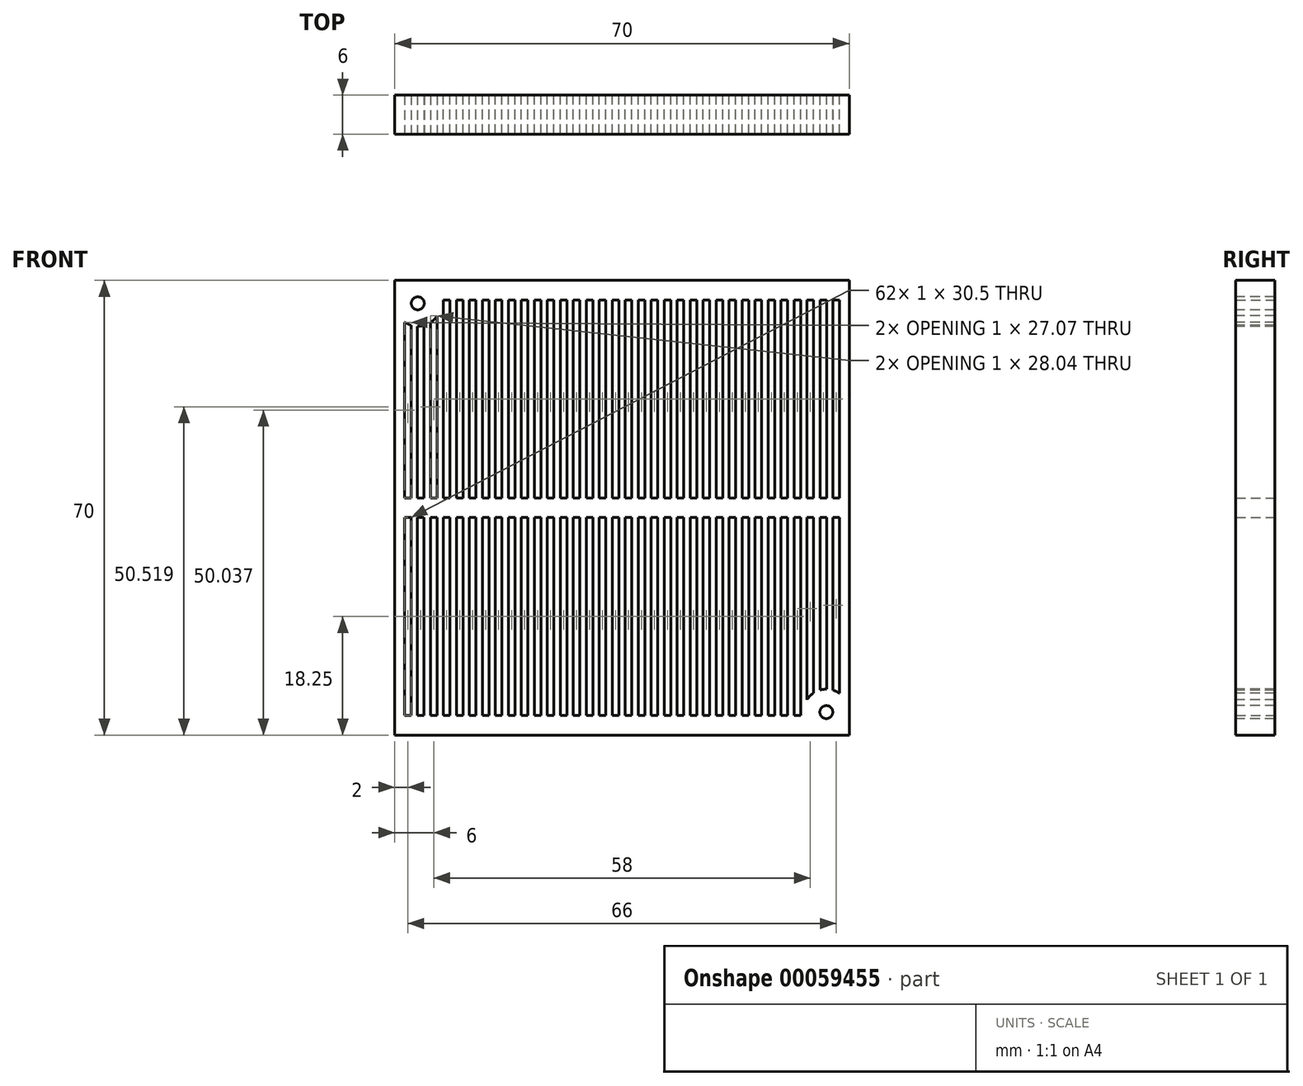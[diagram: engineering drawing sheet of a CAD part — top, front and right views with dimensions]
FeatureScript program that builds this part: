
annotation { "Feature Type Name" : "Feature", "Feature Type Description" : "" }
export const myFeature = defineFeature(function(context is Context, id is Id, definition is map)
    precondition{}
    {
        {
            var Q0;
            Q0=qCreatedBy(makeId("Front.planeOp"),FACE);
            var sketch = newSketch(context, id + "F0", { "sketchPlane" : qUnion([Q0])});
            skLineSegment(sketch, "E0.bottom", {"start": v(0, 70) * mm, "end": v(70, 70) * mm});
            skLineSegment(sketch, "E0.top", {"start": v(0, 0) * mm, "end": v(70, 0) * mm});
            skLineSegment(sketch, "E0.left", {"start": v(0, 70) * mm, "end": v(0, 0) * mm});
            skLineSegment(sketch, "E0.right", {"start": v(70, 70) * mm, "end": v(70, 0) * mm});
            skLineSegment(sketch, "E1.bottom", {"start": v(1.5, 67) * mm, "end": v(2.5, 67) * mm});
            skLineSegment(sketch, "E1.top", {"start": v(1.5, 36.5) * mm, "end": v(2.5, 36.5) * mm});
            skLineSegment(sketch, "E1.left", {"start": v(1.5, 67) * mm, "end": v(1.5, 36.5) * mm});
            skLineSegment(sketch, "E1.right", {"start": v(2.5, 67) * mm, "end": v(2.5, 36.5) * mm});
            skLineSegment(sketch, "E2.bottom", {"start": v(1.5, 33.5) * mm, "end": v(2.5, 33.5) * mm});
            skLineSegment(sketch, "E2.top", {"start": v(1.5, 3) * mm, "end": v(2.5, 3) * mm});
            skLineSegment(sketch, "E2.left", {"start": v(1.5, 33.5) * mm, "end": v(1.5, 3) * mm});
            skLineSegment(sketch, "E2.right", {"start": v(2.5, 33.5) * mm, "end": v(2.5, 3) * mm});
            skLineSegment(sketch, "E3.1.0.0", {"start": v(4.5, 67) * mm, "end": v(4.5, 36.5) * mm});
            skLineSegment(sketch, "E3.1.0.1", {"start": v(4.5, 33.5) * mm, "end": v(4.5, 3) * mm});
            skLineSegment(sketch, "E3.1.0.2", {"start": v(3.5, 33.5) * mm, "end": v(4.5, 33.5) * mm});
            skLineSegment(sketch, "E3.1.0.3", {"start": v(3.5, 33.5) * mm, "end": v(3.5, 3) * mm});
            skLineSegment(sketch, "E3.1.0.4", {"start": v(3.5, 3) * mm, "end": v(4.5, 3) * mm});
            skLineSegment(sketch, "E3.1.0.5", {"start": v(3.5, 67) * mm, "end": v(3.5, 36.5) * mm});
            skLineSegment(sketch, "E3.1.0.6", {"start": v(3.5, 67) * mm, "end": v(4.5, 67) * mm});
            skLineSegment(sketch, "E3.1.0.7", {"start": v(3.5, 36.5) * mm, "end": v(4.5, 36.5) * mm});
            skLineSegment(sketch, "E3.2.0.0", {"start": v(6.5, 67) * mm, "end": v(6.5, 36.5) * mm});
            skLineSegment(sketch, "E3.2.0.1", {"start": v(6.5, 33.5) * mm, "end": v(6.5, 3) * mm});
            skLineSegment(sketch, "E3.2.0.2", {"start": v(5.5, 33.5) * mm, "end": v(6.5, 33.5) * mm});
            skLineSegment(sketch, "E3.2.0.3", {"start": v(5.5, 33.5) * mm, "end": v(5.5, 3) * mm});
            skLineSegment(sketch, "E3.2.0.4", {"start": v(5.5, 3) * mm, "end": v(6.5, 3) * mm});
            skLineSegment(sketch, "E3.2.0.5", {"start": v(5.5, 67) * mm, "end": v(5.5, 36.5) * mm});
            skLineSegment(sketch, "E3.2.0.6", {"start": v(5.5, 67) * mm, "end": v(6.5, 67) * mm});
            skLineSegment(sketch, "E3.2.0.7", {"start": v(5.5, 36.5) * mm, "end": v(6.5, 36.5) * mm});
            skLineSegment(sketch, "E3.3.0.0", {"start": v(8.5, 67) * mm, "end": v(8.5, 36.5) * mm});
            skLineSegment(sketch, "E3.3.0.1", {"start": v(8.5, 33.5) * mm, "end": v(8.5, 3) * mm});
            skLineSegment(sketch, "E3.3.0.2", {"start": v(7.5, 33.5) * mm, "end": v(8.5, 33.5) * mm});
            skLineSegment(sketch, "E3.3.0.3", {"start": v(7.5, 33.5) * mm, "end": v(7.5, 3) * mm});
            skLineSegment(sketch, "E3.3.0.4", {"start": v(7.5, 3) * mm, "end": v(8.5, 3) * mm});
            skLineSegment(sketch, "E3.3.0.5", {"start": v(7.5, 67) * mm, "end": v(7.5, 36.5) * mm});
            skLineSegment(sketch, "E3.3.0.6", {"start": v(7.5, 67) * mm, "end": v(8.5, 67) * mm});
            skLineSegment(sketch, "E3.3.0.7", {"start": v(7.5, 36.5) * mm, "end": v(8.5, 36.5) * mm});
            skLineSegment(sketch, "E3.4.0.0", {"start": v(10.5, 67) * mm, "end": v(10.5, 36.5) * mm});
            skLineSegment(sketch, "E3.4.0.1", {"start": v(10.5, 33.5) * mm, "end": v(10.5, 3) * mm});
            skLineSegment(sketch, "E3.4.0.2", {"start": v(9.5, 33.5) * mm, "end": v(10.5, 33.5) * mm});
            skLineSegment(sketch, "E3.4.0.3", {"start": v(9.5, 33.5) * mm, "end": v(9.5, 3) * mm});
            skLineSegment(sketch, "E3.4.0.4", {"start": v(9.5, 3) * mm, "end": v(10.5, 3) * mm});
            skLineSegment(sketch, "E3.4.0.5", {"start": v(9.5, 67) * mm, "end": v(9.5, 36.5) * mm});
            skLineSegment(sketch, "E3.4.0.6", {"start": v(9.5, 67) * mm, "end": v(10.5, 67) * mm});
            skLineSegment(sketch, "E3.4.0.7", {"start": v(9.5, 36.5) * mm, "end": v(10.5, 36.5) * mm});
            skLineSegment(sketch, "E3.5.0.0", {"start": v(12.5, 67) * mm, "end": v(12.5, 36.5) * mm});
            skLineSegment(sketch, "E3.5.0.1", {"start": v(12.5, 33.5) * mm, "end": v(12.5, 3) * mm});
            skLineSegment(sketch, "E3.5.0.2", {"start": v(11.5, 33.5) * mm, "end": v(12.5, 33.5) * mm});
            skLineSegment(sketch, "E3.5.0.3", {"start": v(11.5, 33.5) * mm, "end": v(11.5, 3) * mm});
            skLineSegment(sketch, "E3.5.0.4", {"start": v(11.5, 3) * mm, "end": v(12.5, 3) * mm});
            skLineSegment(sketch, "E3.5.0.5", {"start": v(11.5, 67) * mm, "end": v(11.5, 36.5) * mm});
            skLineSegment(sketch, "E3.5.0.6", {"start": v(11.5, 67) * mm, "end": v(12.5, 67) * mm});
            skLineSegment(sketch, "E3.5.0.7", {"start": v(11.5, 36.5) * mm, "end": v(12.5, 36.5) * mm});
            skLineSegment(sketch, "E3.6.0.0", {"start": v(14.5, 67) * mm, "end": v(14.5, 36.5) * mm});
            skLineSegment(sketch, "E3.6.0.1", {"start": v(14.5, 33.5) * mm, "end": v(14.5, 3) * mm});
            skLineSegment(sketch, "E3.6.0.2", {"start": v(13.5, 33.5) * mm, "end": v(14.5, 33.5) * mm});
            skLineSegment(sketch, "E3.6.0.3", {"start": v(13.5, 33.5) * mm, "end": v(13.5, 3) * mm});
            skLineSegment(sketch, "E3.6.0.4", {"start": v(13.5, 3) * mm, "end": v(14.5, 3) * mm});
            skLineSegment(sketch, "E3.6.0.5", {"start": v(13.5, 67) * mm, "end": v(13.5, 36.5) * mm});
            skLineSegment(sketch, "E3.6.0.6", {"start": v(13.5, 67) * mm, "end": v(14.5, 67) * mm});
            skLineSegment(sketch, "E3.6.0.7", {"start": v(13.5, 36.5) * mm, "end": v(14.5, 36.5) * mm});
            skLineSegment(sketch, "E3.7.0.0", {"start": v(16.5, 67) * mm, "end": v(16.5, 36.5) * mm});
            skLineSegment(sketch, "E3.7.0.1", {"start": v(16.5, 33.5) * mm, "end": v(16.5, 3) * mm});
            skLineSegment(sketch, "E3.7.0.2", {"start": v(15.5, 33.5) * mm, "end": v(16.5, 33.5) * mm});
            skLineSegment(sketch, "E3.7.0.3", {"start": v(15.5, 33.5) * mm, "end": v(15.5, 3) * mm});
            skLineSegment(sketch, "E3.7.0.4", {"start": v(15.5, 3) * mm, "end": v(16.5, 3) * mm});
            skLineSegment(sketch, "E3.7.0.5", {"start": v(15.5, 67) * mm, "end": v(15.5, 36.5) * mm});
            skLineSegment(sketch, "E3.7.0.6", {"start": v(15.5, 67) * mm, "end": v(16.5, 67) * mm});
            skLineSegment(sketch, "E3.7.0.7", {"start": v(15.5, 36.5) * mm, "end": v(16.5, 36.5) * mm});
            skLineSegment(sketch, "E3.8.0.0", {"start": v(18.5, 67) * mm, "end": v(18.5, 36.5) * mm});
            skLineSegment(sketch, "E3.8.0.1", {"start": v(18.5, 33.5) * mm, "end": v(18.5, 3) * mm});
            skLineSegment(sketch, "E3.8.0.2", {"start": v(17.5, 33.5) * mm, "end": v(18.5, 33.5) * mm});
            skLineSegment(sketch, "E3.8.0.3", {"start": v(17.5, 33.5) * mm, "end": v(17.5, 3) * mm});
            skLineSegment(sketch, "E3.8.0.4", {"start": v(17.5, 3) * mm, "end": v(18.5, 3) * mm});
            skLineSegment(sketch, "E3.8.0.5", {"start": v(17.5, 67) * mm, "end": v(17.5, 36.5) * mm});
            skLineSegment(sketch, "E3.8.0.6", {"start": v(17.5, 67) * mm, "end": v(18.5, 67) * mm});
            skLineSegment(sketch, "E3.8.0.7", {"start": v(17.5, 36.5) * mm, "end": v(18.5, 36.5) * mm});
            skLineSegment(sketch, "E3.9.0.0", {"start": v(20.5, 67) * mm, "end": v(20.5, 36.5) * mm});
            skLineSegment(sketch, "E3.9.0.1", {"start": v(20.5, 33.5) * mm, "end": v(20.5, 3) * mm});
            skLineSegment(sketch, "E3.9.0.2", {"start": v(19.5, 33.5) * mm, "end": v(20.5, 33.5) * mm});
            skLineSegment(sketch, "E3.9.0.3", {"start": v(19.5, 33.5) * mm, "end": v(19.5, 3) * mm});
            skLineSegment(sketch, "E3.9.0.4", {"start": v(19.5, 3) * mm, "end": v(20.5, 3) * mm});
            skLineSegment(sketch, "E3.9.0.5", {"start": v(19.5, 67) * mm, "end": v(19.5, 36.5) * mm});
            skLineSegment(sketch, "E3.9.0.6", {"start": v(19.5, 67) * mm, "end": v(20.5, 67) * mm});
            skLineSegment(sketch, "E3.9.0.7", {"start": v(19.5, 36.5) * mm, "end": v(20.5, 36.5) * mm});
            skLineSegment(sketch, "E3.10.0.0", {"start": v(22.5, 67) * mm, "end": v(22.5, 36.5) * mm});
            skLineSegment(sketch, "E3.10.0.1", {"start": v(22.5, 33.5) * mm, "end": v(22.5, 3) * mm});
            skLineSegment(sketch, "E3.10.0.2", {"start": v(21.5, 33.5) * mm, "end": v(22.5, 33.5) * mm});
            skLineSegment(sketch, "E3.10.0.3", {"start": v(21.5, 33.5) * mm, "end": v(21.5, 3) * mm});
            skLineSegment(sketch, "E3.10.0.4", {"start": v(21.5, 3) * mm, "end": v(22.5, 3) * mm});
            skLineSegment(sketch, "E3.10.0.5", {"start": v(21.5, 67) * mm, "end": v(21.5, 36.5) * mm});
            skLineSegment(sketch, "E3.10.0.6", {"start": v(21.5, 67) * mm, "end": v(22.5, 67) * mm});
            skLineSegment(sketch, "E3.10.0.7", {"start": v(21.5, 36.5) * mm, "end": v(22.5, 36.5) * mm});
            skLineSegment(sketch, "E3.11.0.0", {"start": v(24.5, 67) * mm, "end": v(24.5, 36.5) * mm});
            skLineSegment(sketch, "E3.11.0.1", {"start": v(24.5, 33.5) * mm, "end": v(24.5, 3) * mm});
            skLineSegment(sketch, "E3.11.0.2", {"start": v(23.5, 33.5) * mm, "end": v(24.5, 33.5) * mm});
            skLineSegment(sketch, "E3.11.0.3", {"start": v(23.5, 33.5) * mm, "end": v(23.5, 3) * mm});
            skLineSegment(sketch, "E3.11.0.4", {"start": v(23.5, 3) * mm, "end": v(24.5, 3) * mm});
            skLineSegment(sketch, "E3.11.0.5", {"start": v(23.5, 67) * mm, "end": v(23.5, 36.5) * mm});
            skLineSegment(sketch, "E3.11.0.6", {"start": v(23.5, 67) * mm, "end": v(24.5, 67) * mm});
            skLineSegment(sketch, "E3.11.0.7", {"start": v(23.5, 36.5) * mm, "end": v(24.5, 36.5) * mm});
            skLineSegment(sketch, "E3.12.0.0", {"start": v(26.5, 67) * mm, "end": v(26.5, 36.5) * mm});
            skLineSegment(sketch, "E3.12.0.1", {"start": v(26.5, 33.5) * mm, "end": v(26.5, 3) * mm});
            skLineSegment(sketch, "E3.12.0.2", {"start": v(25.5, 33.5) * mm, "end": v(26.5, 33.5) * mm});
            skLineSegment(sketch, "E3.12.0.3", {"start": v(25.5, 33.5) * mm, "end": v(25.5, 3) * mm});
            skLineSegment(sketch, "E3.12.0.4", {"start": v(25.5, 3) * mm, "end": v(26.5, 3) * mm});
            skLineSegment(sketch, "E3.12.0.5", {"start": v(25.5, 67) * mm, "end": v(25.5, 36.5) * mm});
            skLineSegment(sketch, "E3.12.0.6", {"start": v(25.5, 67) * mm, "end": v(26.5, 67) * mm});
            skLineSegment(sketch, "E3.12.0.7", {"start": v(25.5, 36.5) * mm, "end": v(26.5, 36.5) * mm});
            skLineSegment(sketch, "E3.13.0.0", {"start": v(28.5, 67) * mm, "end": v(28.5, 36.5) * mm});
            skLineSegment(sketch, "E3.13.0.1", {"start": v(28.5, 33.5) * mm, "end": v(28.5, 3) * mm});
            skLineSegment(sketch, "E3.13.0.2", {"start": v(27.5, 33.5) * mm, "end": v(28.5, 33.5) * mm});
            skLineSegment(sketch, "E3.13.0.3", {"start": v(27.5, 33.5) * mm, "end": v(27.5, 3) * mm});
            skLineSegment(sketch, "E3.13.0.4", {"start": v(27.5, 3) * mm, "end": v(28.5, 3) * mm});
            skLineSegment(sketch, "E3.13.0.5", {"start": v(27.5, 67) * mm, "end": v(27.5, 36.5) * mm});
            skLineSegment(sketch, "E3.13.0.6", {"start": v(27.5, 67) * mm, "end": v(28.5, 67) * mm});
            skLineSegment(sketch, "E3.13.0.7", {"start": v(27.5, 36.5) * mm, "end": v(28.5, 36.5) * mm});
            skLineSegment(sketch, "E3.14.0.0", {"start": v(30.5, 67) * mm, "end": v(30.5, 36.5) * mm});
            skLineSegment(sketch, "E3.14.0.1", {"start": v(30.5, 33.5) * mm, "end": v(30.5, 3) * mm});
            skLineSegment(sketch, "E3.14.0.2", {"start": v(29.5, 33.5) * mm, "end": v(30.5, 33.5) * mm});
            skLineSegment(sketch, "E3.14.0.3", {"start": v(29.5, 33.5) * mm, "end": v(29.5, 3) * mm});
            skLineSegment(sketch, "E3.14.0.4", {"start": v(29.5, 3) * mm, "end": v(30.5, 3) * mm});
            skLineSegment(sketch, "E3.14.0.5", {"start": v(29.5, 67) * mm, "end": v(29.5, 36.5) * mm});
            skLineSegment(sketch, "E3.14.0.6", {"start": v(29.5, 67) * mm, "end": v(30.5, 67) * mm});
            skLineSegment(sketch, "E3.14.0.7", {"start": v(29.5, 36.5) * mm, "end": v(30.5, 36.5) * mm});
            skLineSegment(sketch, "E3.15.0.0", {"start": v(32.5, 67) * mm, "end": v(32.5, 36.5) * mm});
            skLineSegment(sketch, "E3.15.0.1", {"start": v(32.5, 33.5) * mm, "end": v(32.5, 3) * mm});
            skLineSegment(sketch, "E3.15.0.2", {"start": v(31.5, 33.5) * mm, "end": v(32.5, 33.5) * mm});
            skLineSegment(sketch, "E3.15.0.3", {"start": v(31.5, 33.5) * mm, "end": v(31.5, 3) * mm});
            skLineSegment(sketch, "E3.15.0.4", {"start": v(31.5, 3) * mm, "end": v(32.5, 3) * mm});
            skLineSegment(sketch, "E3.15.0.5", {"start": v(31.5, 67) * mm, "end": v(31.5, 36.5) * mm});
            skLineSegment(sketch, "E3.15.0.6", {"start": v(31.5, 67) * mm, "end": v(32.5, 67) * mm});
            skLineSegment(sketch, "E3.15.0.7", {"start": v(31.5, 36.5) * mm, "end": v(32.5, 36.5) * mm});
            skLineSegment(sketch, "E3.16.0.0", {"start": v(34.5, 67) * mm, "end": v(34.5, 36.5) * mm});
            skLineSegment(sketch, "E3.16.0.1", {"start": v(34.5, 33.5) * mm, "end": v(34.5, 3) * mm});
            skLineSegment(sketch, "E3.16.0.2", {"start": v(33.5, 33.5) * mm, "end": v(34.5, 33.5) * mm});
            skLineSegment(sketch, "E3.16.0.3", {"start": v(33.5, 33.5) * mm, "end": v(33.5, 3) * mm});
            skLineSegment(sketch, "E3.16.0.4", {"start": v(33.5, 3) * mm, "end": v(34.5, 3) * mm});
            skLineSegment(sketch, "E3.16.0.5", {"start": v(33.5, 67) * mm, "end": v(33.5, 36.5) * mm});
            skLineSegment(sketch, "E3.16.0.6", {"start": v(33.5, 67) * mm, "end": v(34.5, 67) * mm});
            skLineSegment(sketch, "E3.16.0.7", {"start": v(33.5, 36.5) * mm, "end": v(34.5, 36.5) * mm});
            skLineSegment(sketch, "E3.17.0.0", {"start": v(36.5, 67) * mm, "end": v(36.5, 36.5) * mm});
            skLineSegment(sketch, "E3.17.0.1", {"start": v(36.5, 33.5) * mm, "end": v(36.5, 3) * mm});
            skLineSegment(sketch, "E3.17.0.2", {"start": v(35.5, 33.5) * mm, "end": v(36.5, 33.5) * mm});
            skLineSegment(sketch, "E3.17.0.3", {"start": v(35.5, 33.5) * mm, "end": v(35.5, 3) * mm});
            skLineSegment(sketch, "E3.17.0.4", {"start": v(35.5, 3) * mm, "end": v(36.5, 3) * mm});
            skLineSegment(sketch, "E3.17.0.5", {"start": v(35.5, 67) * mm, "end": v(35.5, 36.5) * mm});
            skLineSegment(sketch, "E3.17.0.6", {"start": v(35.5, 67) * mm, "end": v(36.5, 67) * mm});
            skLineSegment(sketch, "E3.17.0.7", {"start": v(35.5, 36.5) * mm, "end": v(36.5, 36.5) * mm});
            skLineSegment(sketch, "E3.18.0.0", {"start": v(38.5, 67) * mm, "end": v(38.5, 36.5) * mm});
            skLineSegment(sketch, "E3.18.0.1", {"start": v(38.5, 33.5) * mm, "end": v(38.5, 3) * mm});
            skLineSegment(sketch, "E3.18.0.2", {"start": v(37.5, 33.5) * mm, "end": v(38.5, 33.5) * mm});
            skLineSegment(sketch, "E3.18.0.3", {"start": v(37.5, 33.5) * mm, "end": v(37.5, 3) * mm});
            skLineSegment(sketch, "E3.18.0.4", {"start": v(37.5, 3) * mm, "end": v(38.5, 3) * mm});
            skLineSegment(sketch, "E3.18.0.5", {"start": v(37.5, 67) * mm, "end": v(37.5, 36.5) * mm});
            skLineSegment(sketch, "E3.18.0.6", {"start": v(37.5, 67) * mm, "end": v(38.5, 67) * mm});
            skLineSegment(sketch, "E3.18.0.7", {"start": v(37.5, 36.5) * mm, "end": v(38.5, 36.5) * mm});
            skLineSegment(sketch, "E3.19.0.0", {"start": v(40.5, 67) * mm, "end": v(40.5, 36.5) * mm});
            skLineSegment(sketch, "E3.19.0.1", {"start": v(40.5, 33.5) * mm, "end": v(40.5, 3) * mm});
            skLineSegment(sketch, "E3.19.0.2", {"start": v(39.5, 33.5) * mm, "end": v(40.5, 33.5) * mm});
            skLineSegment(sketch, "E3.19.0.3", {"start": v(39.5, 33.5) * mm, "end": v(39.5, 3) * mm});
            skLineSegment(sketch, "E3.19.0.4", {"start": v(39.5, 3) * mm, "end": v(40.5, 3) * mm});
            skLineSegment(sketch, "E3.19.0.5", {"start": v(39.5, 67) * mm, "end": v(39.5, 36.5) * mm});
            skLineSegment(sketch, "E3.19.0.6", {"start": v(39.5, 67) * mm, "end": v(40.5, 67) * mm});
            skLineSegment(sketch, "E3.19.0.7", {"start": v(39.5, 36.5) * mm, "end": v(40.5, 36.5) * mm});
            skLineSegment(sketch, "E3.20.0.0", {"start": v(42.5, 67) * mm, "end": v(42.5, 36.5) * mm});
            skLineSegment(sketch, "E3.20.0.1", {"start": v(42.5, 33.5) * mm, "end": v(42.5, 3) * mm});
            skLineSegment(sketch, "E3.20.0.2", {"start": v(41.5, 33.5) * mm, "end": v(42.5, 33.5) * mm});
            skLineSegment(sketch, "E3.20.0.3", {"start": v(41.5, 33.5) * mm, "end": v(41.5, 3) * mm});
            skLineSegment(sketch, "E3.20.0.4", {"start": v(41.5, 3) * mm, "end": v(42.5, 3) * mm});
            skLineSegment(sketch, "E3.20.0.5", {"start": v(41.5, 67) * mm, "end": v(41.5, 36.5) * mm});
            skLineSegment(sketch, "E3.20.0.6", {"start": v(41.5, 67) * mm, "end": v(42.5, 67) * mm});
            skLineSegment(sketch, "E3.20.0.7", {"start": v(41.5, 36.5) * mm, "end": v(42.5, 36.5) * mm});
            skLineSegment(sketch, "E3.21.0.0", {"start": v(44.5, 67) * mm, "end": v(44.5, 36.5) * mm});
            skLineSegment(sketch, "E3.21.0.1", {"start": v(44.5, 33.5) * mm, "end": v(44.5, 3) * mm});
            skLineSegment(sketch, "E3.21.0.2", {"start": v(43.5, 33.5) * mm, "end": v(44.5, 33.5) * mm});
            skLineSegment(sketch, "E3.21.0.3", {"start": v(43.5, 33.5) * mm, "end": v(43.5, 3) * mm});
            skLineSegment(sketch, "E3.21.0.4", {"start": v(43.5, 3) * mm, "end": v(44.5, 3) * mm});
            skLineSegment(sketch, "E3.21.0.5", {"start": v(43.5, 67) * mm, "end": v(43.5, 36.5) * mm});
            skLineSegment(sketch, "E3.21.0.6", {"start": v(43.5, 67) * mm, "end": v(44.5, 67) * mm});
            skLineSegment(sketch, "E3.21.0.7", {"start": v(43.5, 36.5) * mm, "end": v(44.5, 36.5) * mm});
            skLineSegment(sketch, "E3.22.0.0", {"start": v(46.5, 67) * mm, "end": v(46.5, 36.5) * mm});
            skLineSegment(sketch, "E3.22.0.1", {"start": v(46.5, 33.5) * mm, "end": v(46.5, 3) * mm});
            skLineSegment(sketch, "E3.22.0.2", {"start": v(45.5, 33.5) * mm, "end": v(46.5, 33.5) * mm});
            skLineSegment(sketch, "E3.22.0.3", {"start": v(45.5, 33.5) * mm, "end": v(45.5, 3) * mm});
            skLineSegment(sketch, "E3.22.0.4", {"start": v(45.5, 3) * mm, "end": v(46.5, 3) * mm});
            skLineSegment(sketch, "E3.22.0.5", {"start": v(45.5, 67) * mm, "end": v(45.5, 36.5) * mm});
            skLineSegment(sketch, "E3.22.0.6", {"start": v(45.5, 67) * mm, "end": v(46.5, 67) * mm});
            skLineSegment(sketch, "E3.22.0.7", {"start": v(45.5, 36.5) * mm, "end": v(46.5, 36.5) * mm});
            skLineSegment(sketch, "E3.23.0.0", {"start": v(48.5, 67) * mm, "end": v(48.5, 36.5) * mm});
            skLineSegment(sketch, "E3.23.0.1", {"start": v(48.5, 33.5) * mm, "end": v(48.5, 3) * mm});
            skLineSegment(sketch, "E3.23.0.2", {"start": v(47.5, 33.5) * mm, "end": v(48.5, 33.5) * mm});
            skLineSegment(sketch, "E3.23.0.3", {"start": v(47.5, 33.5) * mm, "end": v(47.5, 3) * mm});
            skLineSegment(sketch, "E3.23.0.4", {"start": v(47.5, 3) * mm, "end": v(48.5, 3) * mm});
            skLineSegment(sketch, "E3.23.0.5", {"start": v(47.5, 67) * mm, "end": v(47.5, 36.5) * mm});
            skLineSegment(sketch, "E3.23.0.6", {"start": v(47.5, 67) * mm, "end": v(48.5, 67) * mm});
            skLineSegment(sketch, "E3.23.0.7", {"start": v(47.5, 36.5) * mm, "end": v(48.5, 36.5) * mm});
            skLineSegment(sketch, "E3.24.0.0", {"start": v(50.5, 67) * mm, "end": v(50.5, 36.5) * mm});
            skLineSegment(sketch, "E3.24.0.1", {"start": v(50.5, 33.5) * mm, "end": v(50.5, 3) * mm});
            skLineSegment(sketch, "E3.24.0.2", {"start": v(49.5, 33.5) * mm, "end": v(50.5, 33.5) * mm});
            skLineSegment(sketch, "E3.24.0.3", {"start": v(49.5, 33.5) * mm, "end": v(49.5, 3) * mm});
            skLineSegment(sketch, "E3.24.0.4", {"start": v(49.5, 3) * mm, "end": v(50.5, 3) * mm});
            skLineSegment(sketch, "E3.24.0.5", {"start": v(49.5, 67) * mm, "end": v(49.5, 36.5) * mm});
            skLineSegment(sketch, "E3.24.0.6", {"start": v(49.5, 67) * mm, "end": v(50.5, 67) * mm});
            skLineSegment(sketch, "E3.24.0.7", {"start": v(49.5, 36.5) * mm, "end": v(50.5, 36.5) * mm});
            skLineSegment(sketch, "E3.25.0.0", {"start": v(52.5, 67) * mm, "end": v(52.5, 36.5) * mm});
            skLineSegment(sketch, "E3.25.0.1", {"start": v(52.5, 33.5) * mm, "end": v(52.5, 3) * mm});
            skLineSegment(sketch, "E3.25.0.2", {"start": v(51.5, 33.5) * mm, "end": v(52.5, 33.5) * mm});
            skLineSegment(sketch, "E3.25.0.3", {"start": v(51.5, 33.5) * mm, "end": v(51.5, 3) * mm});
            skLineSegment(sketch, "E3.25.0.4", {"start": v(51.5, 3) * mm, "end": v(52.5, 3) * mm});
            skLineSegment(sketch, "E3.25.0.5", {"start": v(51.5, 67) * mm, "end": v(51.5, 36.5) * mm});
            skLineSegment(sketch, "E3.25.0.6", {"start": v(51.5, 67) * mm, "end": v(52.5, 67) * mm});
            skLineSegment(sketch, "E3.25.0.7", {"start": v(51.5, 36.5) * mm, "end": v(52.5, 36.5) * mm});
            skLineSegment(sketch, "E3.26.0.0", {"start": v(54.5, 67) * mm, "end": v(54.5, 36.5) * mm});
            skLineSegment(sketch, "E3.26.0.1", {"start": v(54.5, 33.5) * mm, "end": v(54.5, 3) * mm});
            skLineSegment(sketch, "E3.26.0.2", {"start": v(53.5, 33.5) * mm, "end": v(54.5, 33.5) * mm});
            skLineSegment(sketch, "E3.26.0.3", {"start": v(53.5, 33.5) * mm, "end": v(53.5, 3) * mm});
            skLineSegment(sketch, "E3.26.0.4", {"start": v(53.5, 3) * mm, "end": v(54.5, 3) * mm});
            skLineSegment(sketch, "E3.26.0.5", {"start": v(53.5, 67) * mm, "end": v(53.5, 36.5) * mm});
            skLineSegment(sketch, "E3.26.0.6", {"start": v(53.5, 67) * mm, "end": v(54.5, 67) * mm});
            skLineSegment(sketch, "E3.26.0.7", {"start": v(53.5, 36.5) * mm, "end": v(54.5, 36.5) * mm});
            skLineSegment(sketch, "E3.27.0.0", {"start": v(56.5, 67) * mm, "end": v(56.5, 36.5) * mm});
            skLineSegment(sketch, "E3.27.0.1", {"start": v(56.5, 33.5) * mm, "end": v(56.5, 3) * mm});
            skLineSegment(sketch, "E3.27.0.2", {"start": v(55.5, 33.5) * mm, "end": v(56.5, 33.5) * mm});
            skLineSegment(sketch, "E3.27.0.3", {"start": v(55.5, 33.5) * mm, "end": v(55.5, 3) * mm});
            skLineSegment(sketch, "E3.27.0.4", {"start": v(55.5, 3) * mm, "end": v(56.5, 3) * mm});
            skLineSegment(sketch, "E3.27.0.5", {"start": v(55.5, 67) * mm, "end": v(55.5, 36.5) * mm});
            skLineSegment(sketch, "E3.27.0.6", {"start": v(55.5, 67) * mm, "end": v(56.5, 67) * mm});
            skLineSegment(sketch, "E3.27.0.7", {"start": v(55.5, 36.5) * mm, "end": v(56.5, 36.5) * mm});
            skLineSegment(sketch, "E3.28.0.0", {"start": v(58.5, 67) * mm, "end": v(58.5, 36.5) * mm});
            skLineSegment(sketch, "E3.28.0.1", {"start": v(58.5, 33.5) * mm, "end": v(58.5, 3) * mm});
            skLineSegment(sketch, "E3.28.0.2", {"start": v(57.5, 33.5) * mm, "end": v(58.5, 33.5) * mm});
            skLineSegment(sketch, "E3.28.0.3", {"start": v(57.5, 33.5) * mm, "end": v(57.5, 3) * mm});
            skLineSegment(sketch, "E3.28.0.4", {"start": v(57.5, 3) * mm, "end": v(58.5, 3) * mm});
            skLineSegment(sketch, "E3.28.0.5", {"start": v(57.5, 67) * mm, "end": v(57.5, 36.5) * mm});
            skLineSegment(sketch, "E3.28.0.6", {"start": v(57.5, 67) * mm, "end": v(58.5, 67) * mm});
            skLineSegment(sketch, "E3.28.0.7", {"start": v(57.5, 36.5) * mm, "end": v(58.5, 36.5) * mm});
            skLineSegment(sketch, "E3.29.0.0", {"start": v(60.5, 67) * mm, "end": v(60.5, 36.5) * mm});
            skLineSegment(sketch, "E3.29.0.1", {"start": v(60.5, 33.5) * mm, "end": v(60.5, 3) * mm});
            skLineSegment(sketch, "E3.29.0.2", {"start": v(59.5, 33.5) * mm, "end": v(60.5, 33.5) * mm});
            skLineSegment(sketch, "E3.29.0.3", {"start": v(59.5, 33.5) * mm, "end": v(59.5, 3) * mm});
            skLineSegment(sketch, "E3.29.0.4", {"start": v(59.5, 3) * mm, "end": v(60.5, 3) * mm});
            skLineSegment(sketch, "E3.29.0.5", {"start": v(59.5, 67) * mm, "end": v(59.5, 36.5) * mm});
            skLineSegment(sketch, "E3.29.0.6", {"start": v(59.5, 67) * mm, "end": v(60.5, 67) * mm});
            skLineSegment(sketch, "E3.29.0.7", {"start": v(59.5, 36.5) * mm, "end": v(60.5, 36.5) * mm});
            skLineSegment(sketch, "E3.30.0.0", {"start": v(62.5, 67) * mm, "end": v(62.5, 36.5) * mm});
            skLineSegment(sketch, "E3.30.0.1", {"start": v(62.5, 33.5) * mm, "end": v(62.5, 3) * mm});
            skLineSegment(sketch, "E3.30.0.2", {"start": v(61.5, 33.5) * mm, "end": v(62.5, 33.5) * mm});
            skLineSegment(sketch, "E3.30.0.3", {"start": v(61.5, 33.5) * mm, "end": v(61.5, 3) * mm});
            skLineSegment(sketch, "E3.30.0.4", {"start": v(61.5, 3) * mm, "end": v(62.5, 3) * mm});
            skLineSegment(sketch, "E3.30.0.5", {"start": v(61.5, 67) * mm, "end": v(61.5, 36.5) * mm});
            skLineSegment(sketch, "E3.30.0.6", {"start": v(61.5, 67) * mm, "end": v(62.5, 67) * mm});
            skLineSegment(sketch, "E3.30.0.7", {"start": v(61.5, 36.5) * mm, "end": v(62.5, 36.5) * mm});
            skLineSegment(sketch, "E3.31.0.0", {"start": v(64.5, 67) * mm, "end": v(64.5, 36.5) * mm});
            skLineSegment(sketch, "E3.31.0.1", {"start": v(64.5, 33.5) * mm, "end": v(64.5, 3) * mm});
            skLineSegment(sketch, "E3.31.0.2", {"start": v(63.5, 33.5) * mm, "end": v(64.5, 33.5) * mm});
            skLineSegment(sketch, "E3.31.0.3", {"start": v(63.5, 33.5) * mm, "end": v(63.5, 3) * mm});
            skLineSegment(sketch, "E3.31.0.4", {"start": v(63.5, 3) * mm, "end": v(64.5, 3) * mm});
            skLineSegment(sketch, "E3.31.0.5", {"start": v(63.5, 67) * mm, "end": v(63.5, 36.5) * mm});
            skLineSegment(sketch, "E3.31.0.6", {"start": v(63.5, 67) * mm, "end": v(64.5, 67) * mm});
            skLineSegment(sketch, "E3.31.0.7", {"start": v(63.5, 36.5) * mm, "end": v(64.5, 36.5) * mm});
            skLineSegment(sketch, "E3.32.0.0", {"start": v(66.5, 67) * mm, "end": v(66.5, 36.5) * mm});
            skLineSegment(sketch, "E3.32.0.1", {"start": v(66.5, 33.5) * mm, "end": v(66.5, 3) * mm});
            skLineSegment(sketch, "E3.32.0.2", {"start": v(65.5, 33.5) * mm, "end": v(66.5, 33.5) * mm});
            skLineSegment(sketch, "E3.32.0.3", {"start": v(65.5, 33.5) * mm, "end": v(65.5, 3) * mm});
            skLineSegment(sketch, "E3.32.0.4", {"start": v(65.5, 3) * mm, "end": v(66.5, 3) * mm});
            skLineSegment(sketch, "E3.32.0.5", {"start": v(65.5, 67) * mm, "end": v(65.5, 36.5) * mm});
            skLineSegment(sketch, "E3.32.0.6", {"start": v(65.5, 67) * mm, "end": v(66.5, 67) * mm});
            skLineSegment(sketch, "E3.32.0.7", {"start": v(65.5, 36.5) * mm, "end": v(66.5, 36.5) * mm});
            skLineSegment(sketch, "E3.33.0.0", {"start": v(68.5, 67) * mm, "end": v(68.5, 36.5) * mm});
            skLineSegment(sketch, "E3.33.0.1", {"start": v(68.5, 33.5) * mm, "end": v(68.5, 3) * mm});
            skLineSegment(sketch, "E3.33.0.2", {"start": v(67.5, 33.5) * mm, "end": v(68.5, 33.5) * mm});
            skLineSegment(sketch, "E3.33.0.3", {"start": v(67.5, 33.5) * mm, "end": v(67.5, 3) * mm});
            skLineSegment(sketch, "E3.33.0.4", {"start": v(67.5, 3) * mm, "end": v(68.5, 3) * mm});
            skLineSegment(sketch, "E3.33.0.5", {"start": v(67.5, 67) * mm, "end": v(67.5, 36.5) * mm});
            skLineSegment(sketch, "E3.33.0.6", {"start": v(67.5, 67) * mm, "end": v(68.5, 67) * mm});
            skLineSegment(sketch, "E3.33.0.7", {"start": v(67.5, 36.5) * mm, "end": v(68.5, 36.5) * mm});
            skLineSegment(sketch, "E3.direction1", {"start": v(2.5, 36.5) * mm, "end": v(4.5, 36.5) * mm, "construction": true});
            skSolve(sketch);
        }
        {
            var Q0;
            Q0 = qSketchRegion(id + "F0", true);
            extrude(context, id + "F1", {"entities" : qUnion([Q0]), "depth" : 6 * mm});
        }
        {
            var Q0;
            Q0=makeQuery(id+"F1.opExtrude","CAP_FACE",FACE,{"disambiguationData":[OSD([sQuery(id+"F0.wireOp",EDGE,"E0.bottom"),sQuery(id+"F0.wireOp",EDGE,"E0.top"),sQuery(id+"F0.wireOp",EDGE,"E0.left"),sQuery(id+"F0.wireOp",EDGE,"E0.right"),sQuery(id+"F0.wireOp",EDGE,"E1.bottom"),sQuery(id+"F0.wireOp",EDGE,"E1.top"),sQuery(id+"F0.wireOp",EDGE,"E1.left"),sQuery(id+"F0.wireOp",EDGE,"E1.right"),sQuery(id+"F0.wireOp",EDGE,"E2.bottom"),sQuery(id+"F0.wireOp",EDGE,"E2.top"),sQuery(id+"F0.wireOp",EDGE,"E2.left"),sQuery(id+"F0.wireOp",EDGE,"E2.right"),sQuery(id+"F0.wireOp",EDGE,"E3.1.0.0"),sQuery(id+"F0.wireOp",EDGE,"E3.1.0.1"),sQuery(id+"F0.wireOp",EDGE,"E3.1.0.2"),sQuery(id+"F0.wireOp",EDGE,"E3.1.0.3"),sQuery(id+"F0.wireOp",EDGE,"E3.1.0.4"),sQuery(id+"F0.wireOp",EDGE,"E3.1.0.5"),sQuery(id+"F0.wireOp",EDGE,"E3.1.0.6"),sQuery(id+"F0.wireOp",EDGE,"E3.1.0.7"),sQuery(id+"F0.wireOp",EDGE,"E3.2.0.0"),sQuery(id+"F0.wireOp",EDGE,"E3.2.0.1"),sQuery(id+"F0.wireOp",EDGE,"E3.2.0.2"),sQuery(id+"F0.wireOp",EDGE,"E3.2.0.3"),sQuery(id+"F0.wireOp",EDGE,"E3.2.0.4"),sQuery(id+"F0.wireOp",EDGE,"E3.2.0.5"),sQuery(id+"F0.wireOp",EDGE,"E3.2.0.6"),sQuery(id+"F0.wireOp",EDGE,"E3.2.0.7"),sQuery(id+"F0.wireOp",EDGE,"E3.3.0.0"),sQuery(id+"F0.wireOp",EDGE,"E3.3.0.1"),sQuery(id+"F0.wireOp",EDGE,"E3.3.0.2"),sQuery(id+"F0.wireOp",EDGE,"E3.3.0.3"),sQuery(id+"F0.wireOp",EDGE,"E3.3.0.4"),sQuery(id+"F0.wireOp",EDGE,"E3.3.0.5"),sQuery(id+"F0.wireOp",EDGE,"E3.3.0.6"),sQuery(id+"F0.wireOp",EDGE,"E3.3.0.7"),sQuery(id+"F0.wireOp",EDGE,"E3.4.0.0"),sQuery(id+"F0.wireOp",EDGE,"E3.4.0.1"),sQuery(id+"F0.wireOp",EDGE,"E3.4.0.2"),sQuery(id+"F0.wireOp",EDGE,"E3.4.0.3"),sQuery(id+"F0.wireOp",EDGE,"E3.4.0.4"),sQuery(id+"F0.wireOp",EDGE,"E3.4.0.5"),sQuery(id+"F0.wireOp",EDGE,"E3.4.0.6"),sQuery(id+"F0.wireOp",EDGE,"E3.4.0.7"),sQuery(id+"F0.wireOp",EDGE,"E3.5.0.0"),sQuery(id+"F0.wireOp",EDGE,"E3.5.0.1"),sQuery(id+"F0.wireOp",EDGE,"E3.5.0.2"),sQuery(id+"F0.wireOp",EDGE,"E3.5.0.3"),sQuery(id+"F0.wireOp",EDGE,"E3.5.0.4"),sQuery(id+"F0.wireOp",EDGE,"E3.5.0.5"),sQuery(id+"F0.wireOp",EDGE,"E3.5.0.6"),sQuery(id+"F0.wireOp",EDGE,"E3.5.0.7"),sQuery(id+"F0.wireOp",EDGE,"E3.6.0.0"),sQuery(id+"F0.wireOp",EDGE,"E3.6.0.1"),sQuery(id+"F0.wireOp",EDGE,"E3.6.0.2"),sQuery(id+"F0.wireOp",EDGE,"E3.6.0.3"),sQuery(id+"F0.wireOp",EDGE,"E3.6.0.4"),sQuery(id+"F0.wireOp",EDGE,"E3.6.0.5"),sQuery(id+"F0.wireOp",EDGE,"E3.6.0.6"),sQuery(id+"F0.wireOp",EDGE,"E3.6.0.7"),sQuery(id+"F0.wireOp",EDGE,"E3.7.0.0"),sQuery(id+"F0.wireOp",EDGE,"E3.7.0.1"),sQuery(id+"F0.wireOp",EDGE,"E3.7.0.2"),sQuery(id+"F0.wireOp",EDGE,"E3.7.0.3"),sQuery(id+"F0.wireOp",EDGE,"E3.7.0.4"),sQuery(id+"F0.wireOp",EDGE,"E3.7.0.5"),sQuery(id+"F0.wireOp",EDGE,"E3.7.0.6"),sQuery(id+"F0.wireOp",EDGE,"E3.7.0.7"),sQuery(id+"F0.wireOp",EDGE,"E3.8.0.0"),sQuery(id+"F0.wireOp",EDGE,"E3.8.0.1"),sQuery(id+"F0.wireOp",EDGE,"E3.8.0.2"),sQuery(id+"F0.wireOp",EDGE,"E3.8.0.3"),sQuery(id+"F0.wireOp",EDGE,"E3.8.0.4"),sQuery(id+"F0.wireOp",EDGE,"E3.8.0.5"),sQuery(id+"F0.wireOp",EDGE,"E3.8.0.6"),sQuery(id+"F0.wireOp",EDGE,"E3.8.0.7"),sQuery(id+"F0.wireOp",EDGE,"E3.9.0.0"),sQuery(id+"F0.wireOp",EDGE,"E3.9.0.1"),sQuery(id+"F0.wireOp",EDGE,"E3.9.0.2"),sQuery(id+"F0.wireOp",EDGE,"E3.9.0.3"),sQuery(id+"F0.wireOp",EDGE,"E3.9.0.4"),sQuery(id+"F0.wireOp",EDGE,"E3.9.0.5"),sQuery(id+"F0.wireOp",EDGE,"E3.9.0.6"),sQuery(id+"F0.wireOp",EDGE,"E3.9.0.7"),sQuery(id+"F0.wireOp",EDGE,"E3.10.0.0"),sQuery(id+"F0.wireOp",EDGE,"E3.10.0.1"),sQuery(id+"F0.wireOp",EDGE,"E3.10.0.2"),sQuery(id+"F0.wireOp",EDGE,"E3.10.0.3"),sQuery(id+"F0.wireOp",EDGE,"E3.10.0.4"),sQuery(id+"F0.wireOp",EDGE,"E3.10.0.5"),sQuery(id+"F0.wireOp",EDGE,"E3.10.0.6"),sQuery(id+"F0.wireOp",EDGE,"E3.10.0.7"),sQuery(id+"F0.wireOp",EDGE,"E3.11.0.0"),sQuery(id+"F0.wireOp",EDGE,"E3.11.0.1"),sQuery(id+"F0.wireOp",EDGE,"E3.11.0.2"),sQuery(id+"F0.wireOp",EDGE,"E3.11.0.3"),sQuery(id+"F0.wireOp",EDGE,"E3.11.0.4"),sQuery(id+"F0.wireOp",EDGE,"E3.11.0.5"),sQuery(id+"F0.wireOp",EDGE,"E3.11.0.6"),sQuery(id+"F0.wireOp",EDGE,"E3.11.0.7"),sQuery(id+"F0.wireOp",EDGE,"E3.12.0.0"),sQuery(id+"F0.wireOp",EDGE,"E3.12.0.1"),sQuery(id+"F0.wireOp",EDGE,"E3.12.0.2"),sQuery(id+"F0.wireOp",EDGE,"E3.12.0.3"),sQuery(id+"F0.wireOp",EDGE,"E3.12.0.4"),sQuery(id+"F0.wireOp",EDGE,"E3.12.0.5"),sQuery(id+"F0.wireOp",EDGE,"E3.12.0.6"),sQuery(id+"F0.wireOp",EDGE,"E3.12.0.7"),sQuery(id+"F0.wireOp",EDGE,"E3.13.0.0"),sQuery(id+"F0.wireOp",EDGE,"E3.13.0.1"),sQuery(id+"F0.wireOp",EDGE,"E3.13.0.2"),sQuery(id+"F0.wireOp",EDGE,"E3.13.0.3"),sQuery(id+"F0.wireOp",EDGE,"E3.13.0.4"),sQuery(id+"F0.wireOp",EDGE,"E3.13.0.5"),sQuery(id+"F0.wireOp",EDGE,"E3.13.0.6"),sQuery(id+"F0.wireOp",EDGE,"E3.13.0.7"),sQuery(id+"F0.wireOp",EDGE,"E3.14.0.0"),sQuery(id+"F0.wireOp",EDGE,"E3.14.0.1"),sQuery(id+"F0.wireOp",EDGE,"E3.14.0.2"),sQuery(id+"F0.wireOp",EDGE,"E3.14.0.3"),sQuery(id+"F0.wireOp",EDGE,"E3.14.0.4"),sQuery(id+"F0.wireOp",EDGE,"E3.14.0.5"),sQuery(id+"F0.wireOp",EDGE,"E3.14.0.6"),sQuery(id+"F0.wireOp",EDGE,"E3.14.0.7"),sQuery(id+"F0.wireOp",EDGE,"E3.15.0.0"),sQuery(id+"F0.wireOp",EDGE,"E3.15.0.1"),sQuery(id+"F0.wireOp",EDGE,"E3.15.0.2"),sQuery(id+"F0.wireOp",EDGE,"E3.15.0.3"),sQuery(id+"F0.wireOp",EDGE,"E3.15.0.4"),sQuery(id+"F0.wireOp",EDGE,"E3.15.0.5"),sQuery(id+"F0.wireOp",EDGE,"E3.15.0.6"),sQuery(id+"F0.wireOp",EDGE,"E3.15.0.7"),sQuery(id+"F0.wireOp",EDGE,"E3.16.0.0"),sQuery(id+"F0.wireOp",EDGE,"E3.16.0.1"),sQuery(id+"F0.wireOp",EDGE,"E3.16.0.2"),sQuery(id+"F0.wireOp",EDGE,"E3.16.0.3"),sQuery(id+"F0.wireOp",EDGE,"E3.16.0.4"),sQuery(id+"F0.wireOp",EDGE,"E3.16.0.5"),sQuery(id+"F0.wireOp",EDGE,"E3.16.0.6"),sQuery(id+"F0.wireOp",EDGE,"E3.16.0.7"),sQuery(id+"F0.wireOp",EDGE,"E3.17.0.0"),sQuery(id+"F0.wireOp",EDGE,"E3.17.0.1"),sQuery(id+"F0.wireOp",EDGE,"E3.17.0.2"),sQuery(id+"F0.wireOp",EDGE,"E3.17.0.3"),sQuery(id+"F0.wireOp",EDGE,"E3.17.0.4"),sQuery(id+"F0.wireOp",EDGE,"E3.17.0.5"),sQuery(id+"F0.wireOp",EDGE,"E3.17.0.6"),sQuery(id+"F0.wireOp",EDGE,"E3.17.0.7"),sQuery(id+"F0.wireOp",EDGE,"E3.18.0.0"),sQuery(id+"F0.wireOp",EDGE,"E3.18.0.1"),sQuery(id+"F0.wireOp",EDGE,"E3.18.0.2"),sQuery(id+"F0.wireOp",EDGE,"E3.18.0.3"),sQuery(id+"F0.wireOp",EDGE,"E3.18.0.4"),sQuery(id+"F0.wireOp",EDGE,"E3.18.0.5"),sQuery(id+"F0.wireOp",EDGE,"E3.18.0.6"),sQuery(id+"F0.wireOp",EDGE,"E3.18.0.7"),sQuery(id+"F0.wireOp",EDGE,"E3.19.0.0"),sQuery(id+"F0.wireOp",EDGE,"E3.19.0.1"),sQuery(id+"F0.wireOp",EDGE,"E3.19.0.2"),sQuery(id+"F0.wireOp",EDGE,"E3.19.0.3"),sQuery(id+"F0.wireOp",EDGE,"E3.19.0.4"),sQuery(id+"F0.wireOp",EDGE,"E3.19.0.5"),sQuery(id+"F0.wireOp",EDGE,"E3.19.0.6"),sQuery(id+"F0.wireOp",EDGE,"E3.19.0.7"),sQuery(id+"F0.wireOp",EDGE,"E3.20.0.0"),sQuery(id+"F0.wireOp",EDGE,"E3.20.0.1"),sQuery(id+"F0.wireOp",EDGE,"E3.20.0.2"),sQuery(id+"F0.wireOp",EDGE,"E3.20.0.3"),sQuery(id+"F0.wireOp",EDGE,"E3.20.0.4"),sQuery(id+"F0.wireOp",EDGE,"E3.20.0.5"),sQuery(id+"F0.wireOp",EDGE,"E3.20.0.6"),sQuery(id+"F0.wireOp",EDGE,"E3.20.0.7"),sQuery(id+"F0.wireOp",EDGE,"E3.21.0.0"),sQuery(id+"F0.wireOp",EDGE,"E3.21.0.1"),sQuery(id+"F0.wireOp",EDGE,"E3.21.0.2"),sQuery(id+"F0.wireOp",EDGE,"E3.21.0.3"),sQuery(id+"F0.wireOp",EDGE,"E3.21.0.4"),sQuery(id+"F0.wireOp",EDGE,"E3.21.0.5"),sQuery(id+"F0.wireOp",EDGE,"E3.21.0.6"),sQuery(id+"F0.wireOp",EDGE,"E3.21.0.7"),sQuery(id+"F0.wireOp",EDGE,"E3.22.0.0"),sQuery(id+"F0.wireOp",EDGE,"E3.22.0.1"),sQuery(id+"F0.wireOp",EDGE,"E3.22.0.2"),sQuery(id+"F0.wireOp",EDGE,"E3.22.0.3"),sQuery(id+"F0.wireOp",EDGE,"E3.22.0.4"),sQuery(id+"F0.wireOp",EDGE,"E3.22.0.5"),sQuery(id+"F0.wireOp",EDGE,"E3.22.0.6"),sQuery(id+"F0.wireOp",EDGE,"E3.22.0.7"),sQuery(id+"F0.wireOp",EDGE,"E3.23.0.0"),sQuery(id+"F0.wireOp",EDGE,"E3.23.0.1"),sQuery(id+"F0.wireOp",EDGE,"E3.23.0.2"),sQuery(id+"F0.wireOp",EDGE,"E3.23.0.3"),sQuery(id+"F0.wireOp",EDGE,"E3.23.0.4"),sQuery(id+"F0.wireOp",EDGE,"E3.23.0.5"),sQuery(id+"F0.wireOp",EDGE,"E3.23.0.6"),sQuery(id+"F0.wireOp",EDGE,"E3.23.0.7"),sQuery(id+"F0.wireOp",EDGE,"E3.24.0.0"),sQuery(id+"F0.wireOp",EDGE,"E3.24.0.1"),sQuery(id+"F0.wireOp",EDGE,"E3.24.0.2"),sQuery(id+"F0.wireOp",EDGE,"E3.24.0.3"),sQuery(id+"F0.wireOp",EDGE,"E3.24.0.4"),sQuery(id+"F0.wireOp",EDGE,"E3.24.0.5"),sQuery(id+"F0.wireOp",EDGE,"E3.24.0.6"),sQuery(id+"F0.wireOp",EDGE,"E3.24.0.7"),sQuery(id+"F0.wireOp",EDGE,"E3.25.0.0"),sQuery(id+"F0.wireOp",EDGE,"E3.25.0.1"),sQuery(id+"F0.wireOp",EDGE,"E3.25.0.2"),sQuery(id+"F0.wireOp",EDGE,"E3.25.0.3"),sQuery(id+"F0.wireOp",EDGE,"E3.25.0.4"),sQuery(id+"F0.wireOp",EDGE,"E3.25.0.5"),sQuery(id+"F0.wireOp",EDGE,"E3.25.0.6"),sQuery(id+"F0.wireOp",EDGE,"E3.25.0.7"),sQuery(id+"F0.wireOp",EDGE,"E3.26.0.0"),sQuery(id+"F0.wireOp",EDGE,"E3.26.0.1"),sQuery(id+"F0.wireOp",EDGE,"E3.26.0.2"),sQuery(id+"F0.wireOp",EDGE,"E3.26.0.3"),sQuery(id+"F0.wireOp",EDGE,"E3.26.0.4"),sQuery(id+"F0.wireOp",EDGE,"E3.26.0.5"),sQuery(id+"F0.wireOp",EDGE,"E3.26.0.6"),sQuery(id+"F0.wireOp",EDGE,"E3.26.0.7"),sQuery(id+"F0.wireOp",EDGE,"E3.27.0.0"),sQuery(id+"F0.wireOp",EDGE,"E3.27.0.1"),sQuery(id+"F0.wireOp",EDGE,"E3.27.0.2"),sQuery(id+"F0.wireOp",EDGE,"E3.27.0.3"),sQuery(id+"F0.wireOp",EDGE,"E3.27.0.4"),sQuery(id+"F0.wireOp",EDGE,"E3.27.0.5"),sQuery(id+"F0.wireOp",EDGE,"E3.27.0.6"),sQuery(id+"F0.wireOp",EDGE,"E3.27.0.7"),sQuery(id+"F0.wireOp",EDGE,"E3.28.0.0"),sQuery(id+"F0.wireOp",EDGE,"E3.28.0.1"),sQuery(id+"F0.wireOp",EDGE,"E3.28.0.2"),sQuery(id+"F0.wireOp",EDGE,"E3.28.0.3"),sQuery(id+"F0.wireOp",EDGE,"E3.28.0.4"),sQuery(id+"F0.wireOp",EDGE,"E3.28.0.5"),sQuery(id+"F0.wireOp",EDGE,"E3.28.0.6"),sQuery(id+"F0.wireOp",EDGE,"E3.28.0.7"),sQuery(id+"F0.wireOp",EDGE,"E3.29.0.0"),sQuery(id+"F0.wireOp",EDGE,"E3.29.0.1"),sQuery(id+"F0.wireOp",EDGE,"E3.29.0.2"),sQuery(id+"F0.wireOp",EDGE,"E3.29.0.3"),sQuery(id+"F0.wireOp",EDGE,"E3.29.0.4"),sQuery(id+"F0.wireOp",EDGE,"E3.29.0.5"),sQuery(id+"F0.wireOp",EDGE,"E3.29.0.6"),sQuery(id+"F0.wireOp",EDGE,"E3.29.0.7"),sQuery(id+"F0.wireOp",EDGE,"E3.30.0.0"),sQuery(id+"F0.wireOp",EDGE,"E3.30.0.1"),sQuery(id+"F0.wireOp",EDGE,"E3.30.0.2"),sQuery(id+"F0.wireOp",EDGE,"E3.30.0.3"),sQuery(id+"F0.wireOp",EDGE,"E3.30.0.4"),sQuery(id+"F0.wireOp",EDGE,"E3.30.0.5"),sQuery(id+"F0.wireOp",EDGE,"E3.30.0.6"),sQuery(id+"F0.wireOp",EDGE,"E3.30.0.7"),sQuery(id+"F0.wireOp",EDGE,"E3.31.0.0"),sQuery(id+"F0.wireOp",EDGE,"E3.31.0.1"),sQuery(id+"F0.wireOp",EDGE,"E3.31.0.2"),sQuery(id+"F0.wireOp",EDGE,"E3.31.0.3"),sQuery(id+"F0.wireOp",EDGE,"E3.31.0.4"),sQuery(id+"F0.wireOp",EDGE,"E3.31.0.5"),sQuery(id+"F0.wireOp",EDGE,"E3.31.0.6"),sQuery(id+"F0.wireOp",EDGE,"E3.31.0.7"),sQuery(id+"F0.wireOp",EDGE,"E3.32.0.0"),sQuery(id+"F0.wireOp",EDGE,"E3.32.0.1"),sQuery(id+"F0.wireOp",EDGE,"E3.32.0.2"),sQuery(id+"F0.wireOp",EDGE,"E3.32.0.3"),sQuery(id+"F0.wireOp",EDGE,"E3.32.0.4"),sQuery(id+"F0.wireOp",EDGE,"E3.32.0.5"),sQuery(id+"F0.wireOp",EDGE,"E3.32.0.6"),sQuery(id+"F0.wireOp",EDGE,"E3.32.0.7"),sQuery(id+"F0.wireOp",EDGE,"E3.33.0.0"),sQuery(id+"F0.wireOp",EDGE,"E3.33.0.1"),sQuery(id+"F0.wireOp",EDGE,"E3.33.0.2"),sQuery(id+"F0.wireOp",EDGE,"E3.33.0.3"),sQuery(id+"F0.wireOp",EDGE,"E3.33.0.4"),sQuery(id+"F0.wireOp",EDGE,"E3.33.0.5"),sQuery(id+"F0.wireOp",EDGE,"E3.33.0.6"),sQuery(id+"F0.wireOp",EDGE,"E3.33.0.7")])],"isStart":false});
            var sketch = newSketch(context, id + "F2", { "sketchPlane" : qUnion([Q0])});
            skLineSegment(sketch, "E4", {"start": v(0, 70) * mm, "end": v(3.54, 66.46) * mm, "construction": true});
            skCircle(sketch, "E5", {"center": v(3.54, 66.46) * mm, "radius": 3.54 * mm});
            skLineSegment(sketch, "E6", {"start": v(0, 0) * mm, "end": v(70, 70) * mm, "construction": true});
            skCircle(sketch, "E7.MirrorC", {"center": v(66.46, 3.54) * mm, "radius": 3.54 * mm});
            skSolve(sketch);
        }
        {
            var Q0;
            Q0 = qSketchRegion(id + "F2", true);
            extrude(context, id + "F3", {"entities" : qUnion([Q0]), "operationType" : NewBodyOperationType.ADD, "oppositeDirection" : true, "depth" : 6 * mm});
        }
        {
            var Q0;
            Q0=makeQuery(id+"F3.boolean.opBoolean","MERGE",FACE,{"derivedFrom":[makeQuery(id+"F1.opExtrude","CAP_FACE",FACE,{"disambiguationData":[OSD([sQuery(id+"F0.wireOp",EDGE,"E0.bottom"),sQuery(id+"F0.wireOp",EDGE,"E0.top"),sQuery(id+"F0.wireOp",EDGE,"E0.left"),sQuery(id+"F0.wireOp",EDGE,"E0.right"),sQuery(id+"F0.wireOp",EDGE,"E1.bottom"),sQuery(id+"F0.wireOp",EDGE,"E1.top"),sQuery(id+"F0.wireOp",EDGE,"E1.left"),sQuery(id+"F0.wireOp",EDGE,"E1.right"),sQuery(id+"F0.wireOp",EDGE,"E2.bottom"),sQuery(id+"F0.wireOp",EDGE,"E2.top"),sQuery(id+"F0.wireOp",EDGE,"E2.left"),sQuery(id+"F0.wireOp",EDGE,"E2.right"),sQuery(id+"F0.wireOp",EDGE,"E3.1.0.0"),sQuery(id+"F0.wireOp",EDGE,"E3.1.0.1"),sQuery(id+"F0.wireOp",EDGE,"E3.1.0.2"),sQuery(id+"F0.wireOp",EDGE,"E3.1.0.3"),sQuery(id+"F0.wireOp",EDGE,"E3.1.0.4"),sQuery(id+"F0.wireOp",EDGE,"E3.1.0.5"),sQuery(id+"F0.wireOp",EDGE,"E3.1.0.6"),sQuery(id+"F0.wireOp",EDGE,"E3.1.0.7"),sQuery(id+"F0.wireOp",EDGE,"E3.2.0.0"),sQuery(id+"F0.wireOp",EDGE,"E3.2.0.1"),sQuery(id+"F0.wireOp",EDGE,"E3.2.0.2"),sQuery(id+"F0.wireOp",EDGE,"E3.2.0.3"),sQuery(id+"F0.wireOp",EDGE,"E3.2.0.4"),sQuery(id+"F0.wireOp",EDGE,"E3.2.0.5"),sQuery(id+"F0.wireOp",EDGE,"E3.2.0.6"),sQuery(id+"F0.wireOp",EDGE,"E3.2.0.7"),sQuery(id+"F0.wireOp",EDGE,"E3.3.0.0"),sQuery(id+"F0.wireOp",EDGE,"E3.3.0.1"),sQuery(id+"F0.wireOp",EDGE,"E3.3.0.2"),sQuery(id+"F0.wireOp",EDGE,"E3.3.0.3"),sQuery(id+"F0.wireOp",EDGE,"E3.3.0.4"),sQuery(id+"F0.wireOp",EDGE,"E3.3.0.5"),sQuery(id+"F0.wireOp",EDGE,"E3.3.0.6"),sQuery(id+"F0.wireOp",EDGE,"E3.3.0.7"),sQuery(id+"F0.wireOp",EDGE,"E3.4.0.0"),sQuery(id+"F0.wireOp",EDGE,"E3.4.0.1"),sQuery(id+"F0.wireOp",EDGE,"E3.4.0.2"),sQuery(id+"F0.wireOp",EDGE,"E3.4.0.3"),sQuery(id+"F0.wireOp",EDGE,"E3.4.0.4"),sQuery(id+"F0.wireOp",EDGE,"E3.4.0.5"),sQuery(id+"F0.wireOp",EDGE,"E3.4.0.6"),sQuery(id+"F0.wireOp",EDGE,"E3.4.0.7"),sQuery(id+"F0.wireOp",EDGE,"E3.5.0.0"),sQuery(id+"F0.wireOp",EDGE,"E3.5.0.1"),sQuery(id+"F0.wireOp",EDGE,"E3.5.0.2"),sQuery(id+"F0.wireOp",EDGE,"E3.5.0.3"),sQuery(id+"F0.wireOp",EDGE,"E3.5.0.4"),sQuery(id+"F0.wireOp",EDGE,"E3.5.0.5"),sQuery(id+"F0.wireOp",EDGE,"E3.5.0.6"),sQuery(id+"F0.wireOp",EDGE,"E3.5.0.7"),sQuery(id+"F0.wireOp",EDGE,"E3.6.0.0"),sQuery(id+"F0.wireOp",EDGE,"E3.6.0.1"),sQuery(id+"F0.wireOp",EDGE,"E3.6.0.2"),sQuery(id+"F0.wireOp",EDGE,"E3.6.0.3"),sQuery(id+"F0.wireOp",EDGE,"E3.6.0.4"),sQuery(id+"F0.wireOp",EDGE,"E3.6.0.5"),sQuery(id+"F0.wireOp",EDGE,"E3.6.0.6"),sQuery(id+"F0.wireOp",EDGE,"E3.6.0.7"),sQuery(id+"F0.wireOp",EDGE,"E3.7.0.0"),sQuery(id+"F0.wireOp",EDGE,"E3.7.0.1"),sQuery(id+"F0.wireOp",EDGE,"E3.7.0.2"),sQuery(id+"F0.wireOp",EDGE,"E3.7.0.3"),sQuery(id+"F0.wireOp",EDGE,"E3.7.0.4"),sQuery(id+"F0.wireOp",EDGE,"E3.7.0.5"),sQuery(id+"F0.wireOp",EDGE,"E3.7.0.6"),sQuery(id+"F0.wireOp",EDGE,"E3.7.0.7"),sQuery(id+"F0.wireOp",EDGE,"E3.8.0.0"),sQuery(id+"F0.wireOp",EDGE,"E3.8.0.1"),sQuery(id+"F0.wireOp",EDGE,"E3.8.0.2"),sQuery(id+"F0.wireOp",EDGE,"E3.8.0.3"),sQuery(id+"F0.wireOp",EDGE,"E3.8.0.4"),sQuery(id+"F0.wireOp",EDGE,"E3.8.0.5"),sQuery(id+"F0.wireOp",EDGE,"E3.8.0.6"),sQuery(id+"F0.wireOp",EDGE,"E3.8.0.7"),sQuery(id+"F0.wireOp",EDGE,"E3.9.0.0"),sQuery(id+"F0.wireOp",EDGE,"E3.9.0.1"),sQuery(id+"F0.wireOp",EDGE,"E3.9.0.2"),sQuery(id+"F0.wireOp",EDGE,"E3.9.0.3"),sQuery(id+"F0.wireOp",EDGE,"E3.9.0.4"),sQuery(id+"F0.wireOp",EDGE,"E3.9.0.5"),sQuery(id+"F0.wireOp",EDGE,"E3.9.0.6"),sQuery(id+"F0.wireOp",EDGE,"E3.9.0.7"),sQuery(id+"F0.wireOp",EDGE,"E3.10.0.0"),sQuery(id+"F0.wireOp",EDGE,"E3.10.0.1"),sQuery(id+"F0.wireOp",EDGE,"E3.10.0.2"),sQuery(id+"F0.wireOp",EDGE,"E3.10.0.3"),sQuery(id+"F0.wireOp",EDGE,"E3.10.0.4"),sQuery(id+"F0.wireOp",EDGE,"E3.10.0.5"),sQuery(id+"F0.wireOp",EDGE,"E3.10.0.6"),sQuery(id+"F0.wireOp",EDGE,"E3.10.0.7"),sQuery(id+"F0.wireOp",EDGE,"E3.11.0.0"),sQuery(id+"F0.wireOp",EDGE,"E3.11.0.1"),sQuery(id+"F0.wireOp",EDGE,"E3.11.0.2"),sQuery(id+"F0.wireOp",EDGE,"E3.11.0.3"),sQuery(id+"F0.wireOp",EDGE,"E3.11.0.4"),sQuery(id+"F0.wireOp",EDGE,"E3.11.0.5"),sQuery(id+"F0.wireOp",EDGE,"E3.11.0.6"),sQuery(id+"F0.wireOp",EDGE,"E3.11.0.7"),sQuery(id+"F0.wireOp",EDGE,"E3.12.0.0"),sQuery(id+"F0.wireOp",EDGE,"E3.12.0.1"),sQuery(id+"F0.wireOp",EDGE,"E3.12.0.2"),sQuery(id+"F0.wireOp",EDGE,"E3.12.0.3"),sQuery(id+"F0.wireOp",EDGE,"E3.12.0.4"),sQuery(id+"F0.wireOp",EDGE,"E3.12.0.5"),sQuery(id+"F0.wireOp",EDGE,"E3.12.0.6"),sQuery(id+"F0.wireOp",EDGE,"E3.12.0.7"),sQuery(id+"F0.wireOp",EDGE,"E3.13.0.0"),sQuery(id+"F0.wireOp",EDGE,"E3.13.0.1"),sQuery(id+"F0.wireOp",EDGE,"E3.13.0.2"),sQuery(id+"F0.wireOp",EDGE,"E3.13.0.3"),sQuery(id+"F0.wireOp",EDGE,"E3.13.0.4"),sQuery(id+"F0.wireOp",EDGE,"E3.13.0.5"),sQuery(id+"F0.wireOp",EDGE,"E3.13.0.6"),sQuery(id+"F0.wireOp",EDGE,"E3.13.0.7"),sQuery(id+"F0.wireOp",EDGE,"E3.14.0.0"),sQuery(id+"F0.wireOp",EDGE,"E3.14.0.1"),sQuery(id+"F0.wireOp",EDGE,"E3.14.0.2"),sQuery(id+"F0.wireOp",EDGE,"E3.14.0.3"),sQuery(id+"F0.wireOp",EDGE,"E3.14.0.4"),sQuery(id+"F0.wireOp",EDGE,"E3.14.0.5"),sQuery(id+"F0.wireOp",EDGE,"E3.14.0.6"),sQuery(id+"F0.wireOp",EDGE,"E3.14.0.7"),sQuery(id+"F0.wireOp",EDGE,"E3.15.0.0"),sQuery(id+"F0.wireOp",EDGE,"E3.15.0.1"),sQuery(id+"F0.wireOp",EDGE,"E3.15.0.2"),sQuery(id+"F0.wireOp",EDGE,"E3.15.0.3"),sQuery(id+"F0.wireOp",EDGE,"E3.15.0.4"),sQuery(id+"F0.wireOp",EDGE,"E3.15.0.5"),sQuery(id+"F0.wireOp",EDGE,"E3.15.0.6"),sQuery(id+"F0.wireOp",EDGE,"E3.15.0.7"),sQuery(id+"F0.wireOp",EDGE,"E3.16.0.0"),sQuery(id+"F0.wireOp",EDGE,"E3.16.0.1"),sQuery(id+"F0.wireOp",EDGE,"E3.16.0.2"),sQuery(id+"F0.wireOp",EDGE,"E3.16.0.3"),sQuery(id+"F0.wireOp",EDGE,"E3.16.0.4"),sQuery(id+"F0.wireOp",EDGE,"E3.16.0.5"),sQuery(id+"F0.wireOp",EDGE,"E3.16.0.6"),sQuery(id+"F0.wireOp",EDGE,"E3.16.0.7"),sQuery(id+"F0.wireOp",EDGE,"E3.17.0.0"),sQuery(id+"F0.wireOp",EDGE,"E3.17.0.1"),sQuery(id+"F0.wireOp",EDGE,"E3.17.0.2"),sQuery(id+"F0.wireOp",EDGE,"E3.17.0.3"),sQuery(id+"F0.wireOp",EDGE,"E3.17.0.4"),sQuery(id+"F0.wireOp",EDGE,"E3.17.0.5"),sQuery(id+"F0.wireOp",EDGE,"E3.17.0.6"),sQuery(id+"F0.wireOp",EDGE,"E3.17.0.7"),sQuery(id+"F0.wireOp",EDGE,"E3.18.0.0"),sQuery(id+"F0.wireOp",EDGE,"E3.18.0.1"),sQuery(id+"F0.wireOp",EDGE,"E3.18.0.2"),sQuery(id+"F0.wireOp",EDGE,"E3.18.0.3"),sQuery(id+"F0.wireOp",EDGE,"E3.18.0.4"),sQuery(id+"F0.wireOp",EDGE,"E3.18.0.5"),sQuery(id+"F0.wireOp",EDGE,"E3.18.0.6"),sQuery(id+"F0.wireOp",EDGE,"E3.18.0.7"),sQuery(id+"F0.wireOp",EDGE,"E3.19.0.0"),sQuery(id+"F0.wireOp",EDGE,"E3.19.0.1"),sQuery(id+"F0.wireOp",EDGE,"E3.19.0.2"),sQuery(id+"F0.wireOp",EDGE,"E3.19.0.3"),sQuery(id+"F0.wireOp",EDGE,"E3.19.0.4"),sQuery(id+"F0.wireOp",EDGE,"E3.19.0.5"),sQuery(id+"F0.wireOp",EDGE,"E3.19.0.6"),sQuery(id+"F0.wireOp",EDGE,"E3.19.0.7"),sQuery(id+"F0.wireOp",EDGE,"E3.20.0.0"),sQuery(id+"F0.wireOp",EDGE,"E3.20.0.1"),sQuery(id+"F0.wireOp",EDGE,"E3.20.0.2"),sQuery(id+"F0.wireOp",EDGE,"E3.20.0.3"),sQuery(id+"F0.wireOp",EDGE,"E3.20.0.4"),sQuery(id+"F0.wireOp",EDGE,"E3.20.0.5"),sQuery(id+"F0.wireOp",EDGE,"E3.20.0.6"),sQuery(id+"F0.wireOp",EDGE,"E3.20.0.7"),sQuery(id+"F0.wireOp",EDGE,"E3.21.0.0"),sQuery(id+"F0.wireOp",EDGE,"E3.21.0.1"),sQuery(id+"F0.wireOp",EDGE,"E3.21.0.2"),sQuery(id+"F0.wireOp",EDGE,"E3.21.0.3"),sQuery(id+"F0.wireOp",EDGE,"E3.21.0.4"),sQuery(id+"F0.wireOp",EDGE,"E3.21.0.5"),sQuery(id+"F0.wireOp",EDGE,"E3.21.0.6"),sQuery(id+"F0.wireOp",EDGE,"E3.21.0.7"),sQuery(id+"F0.wireOp",EDGE,"E3.22.0.0"),sQuery(id+"F0.wireOp",EDGE,"E3.22.0.1"),sQuery(id+"F0.wireOp",EDGE,"E3.22.0.2"),sQuery(id+"F0.wireOp",EDGE,"E3.22.0.3"),sQuery(id+"F0.wireOp",EDGE,"E3.22.0.4"),sQuery(id+"F0.wireOp",EDGE,"E3.22.0.5"),sQuery(id+"F0.wireOp",EDGE,"E3.22.0.6"),sQuery(id+"F0.wireOp",EDGE,"E3.22.0.7"),sQuery(id+"F0.wireOp",EDGE,"E3.23.0.0"),sQuery(id+"F0.wireOp",EDGE,"E3.23.0.1"),sQuery(id+"F0.wireOp",EDGE,"E3.23.0.2"),sQuery(id+"F0.wireOp",EDGE,"E3.23.0.3"),sQuery(id+"F0.wireOp",EDGE,"E3.23.0.4"),sQuery(id+"F0.wireOp",EDGE,"E3.23.0.5"),sQuery(id+"F0.wireOp",EDGE,"E3.23.0.6"),sQuery(id+"F0.wireOp",EDGE,"E3.23.0.7"),sQuery(id+"F0.wireOp",EDGE,"E3.24.0.0"),sQuery(id+"F0.wireOp",EDGE,"E3.24.0.1"),sQuery(id+"F0.wireOp",EDGE,"E3.24.0.2"),sQuery(id+"F0.wireOp",EDGE,"E3.24.0.3"),sQuery(id+"F0.wireOp",EDGE,"E3.24.0.4"),sQuery(id+"F0.wireOp",EDGE,"E3.24.0.5"),sQuery(id+"F0.wireOp",EDGE,"E3.24.0.6"),sQuery(id+"F0.wireOp",EDGE,"E3.24.0.7"),sQuery(id+"F0.wireOp",EDGE,"E3.25.0.0"),sQuery(id+"F0.wireOp",EDGE,"E3.25.0.1"),sQuery(id+"F0.wireOp",EDGE,"E3.25.0.2"),sQuery(id+"F0.wireOp",EDGE,"E3.25.0.3"),sQuery(id+"F0.wireOp",EDGE,"E3.25.0.4"),sQuery(id+"F0.wireOp",EDGE,"E3.25.0.5"),sQuery(id+"F0.wireOp",EDGE,"E3.25.0.6"),sQuery(id+"F0.wireOp",EDGE,"E3.25.0.7"),sQuery(id+"F0.wireOp",EDGE,"E3.26.0.0"),sQuery(id+"F0.wireOp",EDGE,"E3.26.0.1"),sQuery(id+"F0.wireOp",EDGE,"E3.26.0.2"),sQuery(id+"F0.wireOp",EDGE,"E3.26.0.3"),sQuery(id+"F0.wireOp",EDGE,"E3.26.0.4"),sQuery(id+"F0.wireOp",EDGE,"E3.26.0.5"),sQuery(id+"F0.wireOp",EDGE,"E3.26.0.6"),sQuery(id+"F0.wireOp",EDGE,"E3.26.0.7"),sQuery(id+"F0.wireOp",EDGE,"E3.27.0.0"),sQuery(id+"F0.wireOp",EDGE,"E3.27.0.1"),sQuery(id+"F0.wireOp",EDGE,"E3.27.0.2"),sQuery(id+"F0.wireOp",EDGE,"E3.27.0.3"),sQuery(id+"F0.wireOp",EDGE,"E3.27.0.4"),sQuery(id+"F0.wireOp",EDGE,"E3.27.0.5"),sQuery(id+"F0.wireOp",EDGE,"E3.27.0.6"),sQuery(id+"F0.wireOp",EDGE,"E3.27.0.7"),sQuery(id+"F0.wireOp",EDGE,"E3.28.0.0"),sQuery(id+"F0.wireOp",EDGE,"E3.28.0.1"),sQuery(id+"F0.wireOp",EDGE,"E3.28.0.2"),sQuery(id+"F0.wireOp",EDGE,"E3.28.0.3"),sQuery(id+"F0.wireOp",EDGE,"E3.28.0.4"),sQuery(id+"F0.wireOp",EDGE,"E3.28.0.5"),sQuery(id+"F0.wireOp",EDGE,"E3.28.0.6"),sQuery(id+"F0.wireOp",EDGE,"E3.28.0.7"),sQuery(id+"F0.wireOp",EDGE,"E3.29.0.0"),sQuery(id+"F0.wireOp",EDGE,"E3.29.0.1"),sQuery(id+"F0.wireOp",EDGE,"E3.29.0.2"),sQuery(id+"F0.wireOp",EDGE,"E3.29.0.3"),sQuery(id+"F0.wireOp",EDGE,"E3.29.0.4"),sQuery(id+"F0.wireOp",EDGE,"E3.29.0.5"),sQuery(id+"F0.wireOp",EDGE,"E3.29.0.6"),sQuery(id+"F0.wireOp",EDGE,"E3.29.0.7"),sQuery(id+"F0.wireOp",EDGE,"E3.30.0.0"),sQuery(id+"F0.wireOp",EDGE,"E3.30.0.1"),sQuery(id+"F0.wireOp",EDGE,"E3.30.0.2"),sQuery(id+"F0.wireOp",EDGE,"E3.30.0.3"),sQuery(id+"F0.wireOp",EDGE,"E3.30.0.4"),sQuery(id+"F0.wireOp",EDGE,"E3.30.0.5"),sQuery(id+"F0.wireOp",EDGE,"E3.30.0.6"),sQuery(id+"F0.wireOp",EDGE,"E3.30.0.7"),sQuery(id+"F0.wireOp",EDGE,"E3.31.0.0"),sQuery(id+"F0.wireOp",EDGE,"E3.31.0.1"),sQuery(id+"F0.wireOp",EDGE,"E3.31.0.2"),sQuery(id+"F0.wireOp",EDGE,"E3.31.0.3"),sQuery(id+"F0.wireOp",EDGE,"E3.31.0.4"),sQuery(id+"F0.wireOp",EDGE,"E3.31.0.5"),sQuery(id+"F0.wireOp",EDGE,"E3.31.0.6"),sQuery(id+"F0.wireOp",EDGE,"E3.31.0.7"),sQuery(id+"F0.wireOp",EDGE,"E3.32.0.0"),sQuery(id+"F0.wireOp",EDGE,"E3.32.0.1"),sQuery(id+"F0.wireOp",EDGE,"E3.32.0.2"),sQuery(id+"F0.wireOp",EDGE,"E3.32.0.3"),sQuery(id+"F0.wireOp",EDGE,"E3.32.0.4"),sQuery(id+"F0.wireOp",EDGE,"E3.32.0.5"),sQuery(id+"F0.wireOp",EDGE,"E3.32.0.6"),sQuery(id+"F0.wireOp",EDGE,"E3.32.0.7"),sQuery(id+"F0.wireOp",EDGE,"E3.33.0.0"),sQuery(id+"F0.wireOp",EDGE,"E3.33.0.1"),sQuery(id+"F0.wireOp",EDGE,"E3.33.0.2"),sQuery(id+"F0.wireOp",EDGE,"E3.33.0.3"),sQuery(id+"F0.wireOp",EDGE,"E3.33.0.4"),sQuery(id+"F0.wireOp",EDGE,"E3.33.0.5"),sQuery(id+"F0.wireOp",EDGE,"E3.33.0.6"),sQuery(id+"F0.wireOp",EDGE,"E3.33.0.7")])],"isStart":false}),makeQuery(id+"F3.opExtrude","CAP_FACE",FACE,{"disambiguationData":[OSD([sQuery(id+"F2.wireOp",EDGE,"E5")])],"isStart":true}),makeQuery(id+"F3.opExtrude","CAP_FACE",FACE,{"disambiguationData":[OSD([sQuery(id+"F2.wireOp",EDGE,"E7.MirrorC")])],"isStart":true})]});
            var sketch = newSketch(context, id + "F4", { "sketchPlane" : qUnion([Q0])});
            skCircle(sketch, "E8", {"center": v(3.54, 66.46) * mm, "radius": 1 * mm});
            skCircle(sketch, "E9", {"center": v(66.46, 3.54) * mm, "radius": 1 * mm});
            skSolve(sketch);
        }
        {
            var Q0;
            Q0 = qSketchRegion(id + "F4", true);
            extrude(context, id + "F5", {"entities" : qUnion([Q0]), "operationType" : NewBodyOperationType.REMOVE, "oppositeDirection" : true, "depth" : 25 * mm});
        }
    });
